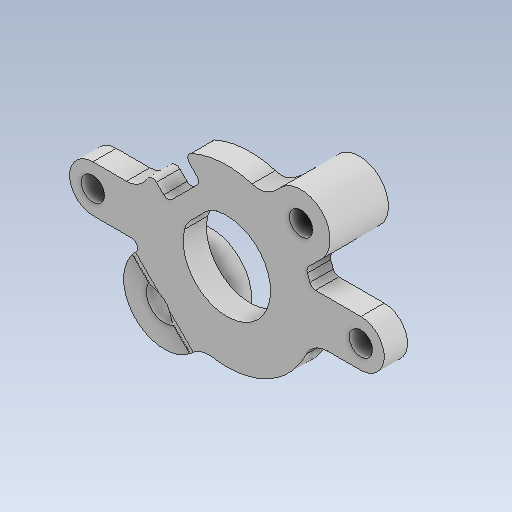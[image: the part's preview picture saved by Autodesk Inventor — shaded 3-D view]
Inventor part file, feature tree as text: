
AUTODESK INVENTOR PART (.ipt)
format: ipt  version: 2023 (Build 270158000, 158)  size: 309,248 bytes
history: native  units: mm
features: sketch x5, other x3
ambient origin geometry x8: Origin, YZ Plane, XZ Plane, XY Plane, X Axis, Y Axis, Z Axis, Center Point
bodies: Solid1 (feature_tree)
feature tree (8):
  other  "encoder_holder_2.ipt"
  other  "Solid1::encoder_holder_2.ipt"
  other  "TaggingFeature1"
  sketch  "Sketch1"  dims[d0=10.0mm]
  sketch  "Sketch2"
  sketch  "Sketch3"
  sketch  "Sketch4"
  sketch  "Sketch5"
